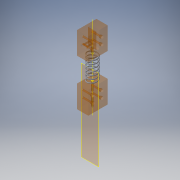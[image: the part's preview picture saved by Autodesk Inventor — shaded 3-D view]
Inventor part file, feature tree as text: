
AUTODESK INVENTOR PART (.ipt)
format: ipt  version: 2016 (Build 200138000, 138)  size: 476,160 bytes
history: native  units: in
note: dims shown in document units (in); Inventor stores cm internally (conversion verified against a paired STEP export)
features: other x5, surface_op x2, plane x1, helix x1, sketch x1
ambient origin geometry x8: Origin, YZ Plane, XZ Plane, XY Plane, X Axis, Y Axis, Z Axis, Center Point
bodies: Solid1 (feature_tree)
feature tree (10):
  other  "Work Axis1"
  other  "Work Point1"
  other  "Work Point2"
  plane  "Work Plane1"
  helix  "Coil1"  [1 undecoded]
  sketch  "Sketch1"  dims[d1=0.429in d2=1.0858in d3=1.0in d4=1.0058in d5=2.7559in d6=0.0in d7=90.0deg d8=90.0deg d9=0.0in d10=0.0in]
  surface_op  "Surface1"
  surface_op  "Surface2"
  other  "Srf1"
  other  "Srf2"
note: 1 required parameter value undecoded (feature->parameter linkage not recoverable at this tier; creation-order binding heuristic only, values carry confidence <= 0.55)
